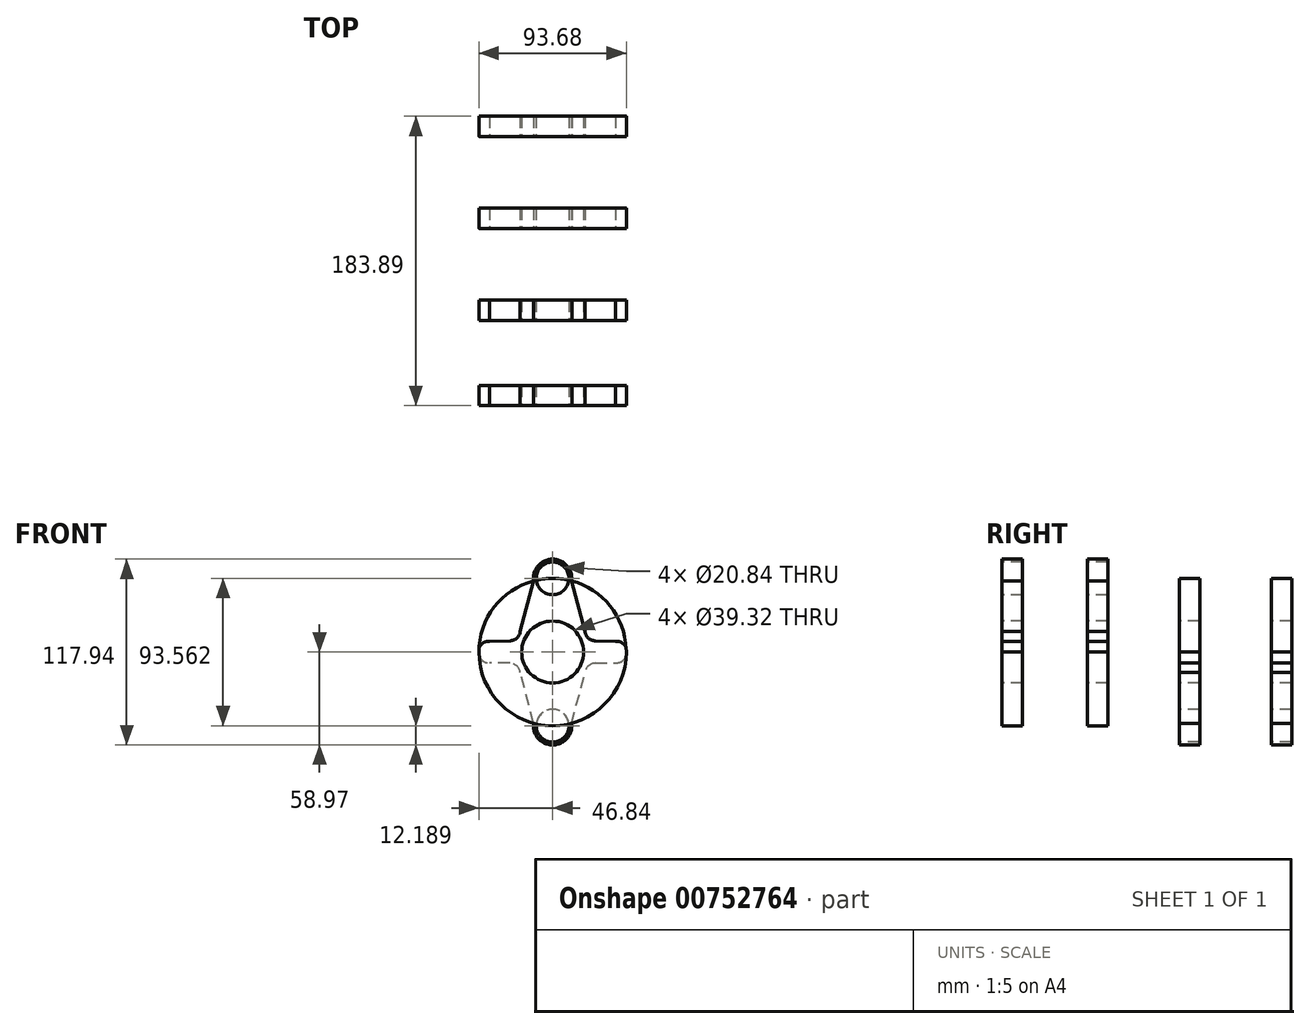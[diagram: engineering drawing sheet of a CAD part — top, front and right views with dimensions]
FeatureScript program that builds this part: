
annotation { "Feature Type Name" : "Feature", "Feature Type Description" : "" }
export const myFeature = defineFeature(function(context is Context, id is Id, definition is map)
    precondition{}
    {
        {
            var Q0;
            Q0=qCreatedBy(makeId("Front.planeOp"),FACE);
            var sketch = newSketch(context, id + "F0", { "sketchPlane" : qUnion([Q0])});
            skArc(sketch, "E0", {"start": v(46.74, -1.9) * mm, "mid": v(33.75, 32.4) * mm, "end": v(0, 46.78) * mm});
            skArc(sketch, "E1", {"start": v(0, -58.97) * mm, "mid": v(9.17, -54.82) * mm, "end": v(12.09, -45.2) * mm});
            skLineSegment(sketch, "E2", {"start": v(12.09, -45.2) * mm, "end": v(20.58, -13.1) * mm});
            skArc(sketch, "E3", {"start": v(27.2, -7.05) * mm, "mid": v(22.75, -8.83) * mm, "end": v(20.58, -13.1) * mm});
            skPoint(sketch, "E3.first.point", {"position": v(34.1, -13.1) * mm});
            skPoint(sketch, "E3.third.point", {"position": v(27.2, -7.05) * mm});
            skLineSegment(sketch, "E4", {"start": v(27.2, -7.05) * mm, "end": v(39.9, -6.78) * mm});
            skArc(sketch, "E5", {"start": v(39.9, -6.78) * mm, "mid": v(45.05, -5.12) * mm, "end": v(46.78, 0) * mm});
            skPoint(sketch, "E5.second.point", {"position": v(42.16, 5.04) * mm});
            skPoint(sketch, "E5.third.point", {"position": v(46.78, 0) * mm});
            skPoint(sketch, "E6", {"position": v(0, 46.78) * mm});
            skPoint(sketch, "E7", {"position": v(0, -58.97) * mm});
            skArc(sketch, "E8.MirrorCS", {"start": v(-46.74, -1.9) * mm, "mid": v(-33.75, 32.4) * mm, "end": v(0, 46.78) * mm});
            skArc(sketch, "E9.MirrorCS", {"start": v(-39.9, -6.78) * mm, "mid": v(-45.05, -5.12) * mm, "end": v(-46.78, 0) * mm});
            skLineSegment(sketch, "E10.MirrorCS", {"start": v(-27.2, -7.05) * mm, "end": v(-39.9, -6.78) * mm});
            skPoint(sketch, "E11.MirrorP", {"position": v(-27.2, -7.05) * mm});
            skLineSegment(sketch, "E12.MirrorCS", {"start": v(-12.09, -45.2) * mm, "end": v(-20.58, -13.1) * mm});
            skArc(sketch, "E13.MirrorCS", {"start": v(0, -58.97) * mm, "mid": v(-9.17, -54.82) * mm, "end": v(-12.09, -45.2) * mm});
            skArc(sketch, "E14.MirrorCS", {"start": v(-27.2, -7.05) * mm, "mid": v(-22.75, -8.83) * mm, "end": v(-20.58, -13.1) * mm});
            skCircle(sketch, "E15", {"center": v(0, 0) * mm, "radius": 16.49 * mm});
            skCircle(sketch, "E16", {"center": v(0, -46.78) * mm, "radius": 8.57 * mm});
            skCircle(sketch, "E17", {"center": v(0, 0) * mm, "radius": 19.66 * mm});
            skCircle(sketch, "E18", {"center": v(0, -46.78) * mm, "radius": 10.42 * mm});
            skSolve(sketch);
        }
        {
            var Q0;
            Q0 = qSketchRegion(id + "F0", true);
            extrude(context, id + "F1", {"entities" : qUnion([Q0]), "oppositeDirection" : true, "depth" : 12.95 * mm, "offsetDistance" : 25.4 * mm});
        }
        {
            var Q0;
            Q0=sQuery(id+"F0.wireOp",EDGE,"E17");
            var Q1;
            Q1=sQuery(id+"F0.wireOp",EDGE,"E15");
            extrude(context, id + "F2", {"bodyType" : ToolBodyType.SURFACE, "surfaceEntities" : qUnion([Q0, Q1]), "depth" : 44.96 * mm, "offsetDistance" : 25.4 * mm});
        }
        {
            var Q0;
            Q0=sQuery(id+"F0.wireOp",EDGE,"E16");
            var Q1;
            Q1=sQuery(id+"F0.wireOp",EDGE,"E18");
            extrude(context, id + "F3", {"bodyType" : ToolBodyType.SURFACE, "surfaceEntities" : qUnion([Q0, Q1]), "oppositeDirection" : true, "depth" : 60.96 * mm, "offsetDistance" : 25.4 * mm});
        }
        {
            var Q0;
            Q0=makeQuery(id+"F1.opExtrude","SWEPT_BODY",BODY,{"disambiguationData":[OSD([sQuery(id+"F0.wireOp",EDGE,"E0"),sQuery(id+"F0.wireOp",EDGE,"E1"),sQuery(id+"F0.wireOp",EDGE,"E2"),sQuery(id+"F0.wireOp",EDGE,"E3"),sQuery(id+"F0.wireOp",EDGE,"E4"),sQuery(id+"F0.wireOp",EDGE,"E5"),sQuery(id+"F0.wireOp",EDGE,"E8.MirrorCS"),sQuery(id+"F0.wireOp",EDGE,"E9.MirrorCS"),sQuery(id+"F0.wireOp",EDGE,"E10.MirrorCS"),sQuery(id+"F0.wireOp",EDGE,"E12.MirrorCS"),sQuery(id+"F0.wireOp",EDGE,"E13.MirrorCS"),sQuery(id+"F0.wireOp",EDGE,"E14.MirrorCS"),sQuery(id+"F0.wireOp",EDGE,"E17"),sQuery(id+"F0.wireOp",EDGE,"E18")])]});
            var Q1;
            Q1=makeQuery(id+"F2.opExtrude","SWEPT_BODY",BODY,{"disambiguationData":[OSD([sQuery(id+"F0.wireOp",EDGE,"E17")])]});
            var Q2;
            Q2=makeQuery(id+"F1.opExtrude","SWEPT_FACE",FACE,{"disambiguationData":[OSD([sQuery(id+"F0.wireOp",EDGE,"E0"),sQuery(id+"F0.wireOp",EDGE,"E8.MirrorCS")])]});
            var Q3;
            Q3=makeQuery(id+"F2.opExtrude","SWEPT_FACE",FACE,{"disambiguationData":[OSD([sQuery(id+"F0.wireOp",EDGE,"E17")])]});
            transform(context, id + "F4", {"entities" : qUnion([Q0, Q1]), "transformType" : TransformType.TRANSLATION_DISTANCE, "transformDirection" : qUnion([Q2, Q3]), "distance" : 58.42 * mm, "makeCopy" : true});
        }
        {
            var Q0;
            Q0=makeQuery(id+"F1.opExtrude","SWEPT_BODY",BODY,{"disambiguationData":[OSD([sQuery(id+"F0.wireOp",EDGE,"E0"),sQuery(id+"F0.wireOp",EDGE,"E1"),sQuery(id+"F0.wireOp",EDGE,"E2"),sQuery(id+"F0.wireOp",EDGE,"E3"),sQuery(id+"F0.wireOp",EDGE,"E4"),sQuery(id+"F0.wireOp",EDGE,"E5"),sQuery(id+"F0.wireOp",EDGE,"E8.MirrorCS"),sQuery(id+"F0.wireOp",EDGE,"E9.MirrorCS"),sQuery(id+"F0.wireOp",EDGE,"E10.MirrorCS"),sQuery(id+"F0.wireOp",EDGE,"E12.MirrorCS"),sQuery(id+"F0.wireOp",EDGE,"E13.MirrorCS"),sQuery(id+"F0.wireOp",EDGE,"E14.MirrorCS"),sQuery(id+"F0.wireOp",EDGE,"E17"),sQuery(id+"F0.wireOp",EDGE,"E18")])]});
            var Q1;
            Q1=makeQuery(id+"F4.opPattern","COPY",FACE,{"derivedFrom":makeQuery(id+"F1.opExtrude","SWEPT_FACE",FACE,{"disambiguationData":[OSD([sQuery(id+"F0.wireOp",EDGE,"E0"),sQuery(id+"F0.wireOp",EDGE,"E8.MirrorCS")])]}),"instanceName":"1"});
            transform(context, id + "F5", {"entities" : qUnion([Q0]), "transformType" : TransformType.TRANSLATION_DISTANCE, "transformDirection" : qUnion([Q1]), "distance" : 116.84 * mm, "makeCopy" : true});
        }
        {
            var Q0;
            Q0=makeQuery(id+"F4.opPattern","COPY",BODY,{"derivedFrom":makeQuery(id+"F2.opExtrude","SWEPT_BODY",BODY,{"disambiguationData":[OSD([sQuery(id+"F0.wireOp",EDGE,"E17")])]}),"instanceName":"1"});
            var Q1;
            Q1=makeQuery(id+"F4.opPattern","COPY",FACE,{"derivedFrom":makeQuery(id+"F2.opExtrude","SWEPT_FACE",FACE,{"disambiguationData":[OSD([sQuery(id+"F0.wireOp",EDGE,"E17")])]}),"instanceName":"1"});
            transform(context, id + "F6", {"entities" : qUnion([Q0]), "transformType" : TransformType.TRANSLATION_DISTANCE, "transformDirection" : qUnion([Q1]), "distance" : 54.86 * mm, "makeCopy" : true});
        }
        {
            var Q0;
            Q0=makeQuery(id+"F5.opPattern","COPY",BODY,{"derivedFrom":makeQuery(id+"F1.opExtrude","SWEPT_BODY",BODY,{"disambiguationData":[OSD([sQuery(id+"F0.wireOp",EDGE,"E0"),sQuery(id+"F0.wireOp",EDGE,"E1"),sQuery(id+"F0.wireOp",EDGE,"E2"),sQuery(id+"F0.wireOp",EDGE,"E3"),sQuery(id+"F0.wireOp",EDGE,"E4"),sQuery(id+"F0.wireOp",EDGE,"E5"),sQuery(id+"F0.wireOp",EDGE,"E8.MirrorCS"),sQuery(id+"F0.wireOp",EDGE,"E9.MirrorCS"),sQuery(id+"F0.wireOp",EDGE,"E10.MirrorCS"),sQuery(id+"F0.wireOp",EDGE,"E12.MirrorCS"),sQuery(id+"F0.wireOp",EDGE,"E13.MirrorCS"),sQuery(id+"F0.wireOp",EDGE,"E14.MirrorCS"),sQuery(id+"F0.wireOp",EDGE,"E17"),sQuery(id+"F0.wireOp",EDGE,"E18")])]}),"instanceName":"1"});
            var Q1;
            Q1=makeQuery(id+"F5.opPattern","COPY",FACE,{"derivedFrom":makeQuery(id+"F1.opExtrude","SWEPT_FACE",FACE,{"disambiguationData":[OSD([sQuery(id+"F0.wireOp",EDGE,"E0"),sQuery(id+"F0.wireOp",EDGE,"E8.MirrorCS")])]}),"instanceName":"1"});
            transform(context, id + "F7", {"entities" : qUnion([Q0]), "transformType" : TransformType.TRANSLATION_DISTANCE, "transformDirection" : qUnion([Q1]), "distance" : 54.1 * mm, "makeCopy" : true});
        }
        {
            var Q0;
            Q0=makeQuery(id+"F6.opPattern","COPY",BODY,{"derivedFrom":makeQuery(id+"F4.opPattern","COPY",BODY,{"derivedFrom":makeQuery(id+"F2.opExtrude","SWEPT_BODY",BODY,{"disambiguationData":[OSD([sQuery(id+"F0.wireOp",EDGE,"E17")])]}),"instanceName":"1"}),"instanceName":"1"});
            var Q1;
            Q1=makeQuery(id+"F4.opPattern","COPY",BODY,{"derivedFrom":makeQuery(id+"F2.opExtrude","SWEPT_BODY",BODY,{"disambiguationData":[OSD([sQuery(id+"F0.wireOp",EDGE,"E17")])]}),"instanceName":"1"});
            var Q2;
            Q2=makeQuery(id+"F5.opPattern","COPY",BODY,{"derivedFrom":makeQuery(id+"F1.opExtrude","SWEPT_BODY",BODY,{"disambiguationData":[OSD([sQuery(id+"F0.wireOp",EDGE,"E0"),sQuery(id+"F0.wireOp",EDGE,"E1"),sQuery(id+"F0.wireOp",EDGE,"E2"),sQuery(id+"F0.wireOp",EDGE,"E3"),sQuery(id+"F0.wireOp",EDGE,"E4"),sQuery(id+"F0.wireOp",EDGE,"E5"),sQuery(id+"F0.wireOp",EDGE,"E8.MirrorCS"),sQuery(id+"F0.wireOp",EDGE,"E9.MirrorCS"),sQuery(id+"F0.wireOp",EDGE,"E10.MirrorCS"),sQuery(id+"F0.wireOp",EDGE,"E12.MirrorCS"),sQuery(id+"F0.wireOp",EDGE,"E13.MirrorCS"),sQuery(id+"F0.wireOp",EDGE,"E14.MirrorCS"),sQuery(id+"F0.wireOp",EDGE,"E17"),sQuery(id+"F0.wireOp",EDGE,"E18")])]}),"instanceName":"1"});
            var Q3;
            Q3=makeQuery(id+"F7.opPattern","COPY",BODY,{"derivedFrom":makeQuery(id+"F5.opPattern","COPY",BODY,{"derivedFrom":makeQuery(id+"F1.opExtrude","SWEPT_BODY",BODY,{"disambiguationData":[OSD([sQuery(id+"F0.wireOp",EDGE,"E0"),sQuery(id+"F0.wireOp",EDGE,"E1"),sQuery(id+"F0.wireOp",EDGE,"E2"),sQuery(id+"F0.wireOp",EDGE,"E3"),sQuery(id+"F0.wireOp",EDGE,"E4"),sQuery(id+"F0.wireOp",EDGE,"E5"),sQuery(id+"F0.wireOp",EDGE,"E8.MirrorCS"),sQuery(id+"F0.wireOp",EDGE,"E9.MirrorCS"),sQuery(id+"F0.wireOp",EDGE,"E10.MirrorCS"),sQuery(id+"F0.wireOp",EDGE,"E12.MirrorCS"),sQuery(id+"F0.wireOp",EDGE,"E13.MirrorCS"),sQuery(id+"F0.wireOp",EDGE,"E14.MirrorCS"),sQuery(id+"F0.wireOp",EDGE,"E17"),sQuery(id+"F0.wireOp",EDGE,"E18")])]}),"instanceName":"1"}),"instanceName":"1"});
            var Q4;
            Q4=makeQuery(id+"F4.opPattern","COPY",FACE,{"derivedFrom":makeQuery(id+"F2.opExtrude","SWEPT_FACE",FACE,{"disambiguationData":[OSD([sQuery(id+"F0.wireOp",EDGE,"E17")])]}),"instanceName":"1"});
            transform(context, id + "F8", {"entities" : qUnion([Q0, Q1, Q2, Q3]), "transformType" : TransformType.ROTATION, "transformAxis" : qUnion([Q4]), "angle" : 180 * degree, "makeCopy" : false});
        }
    });
